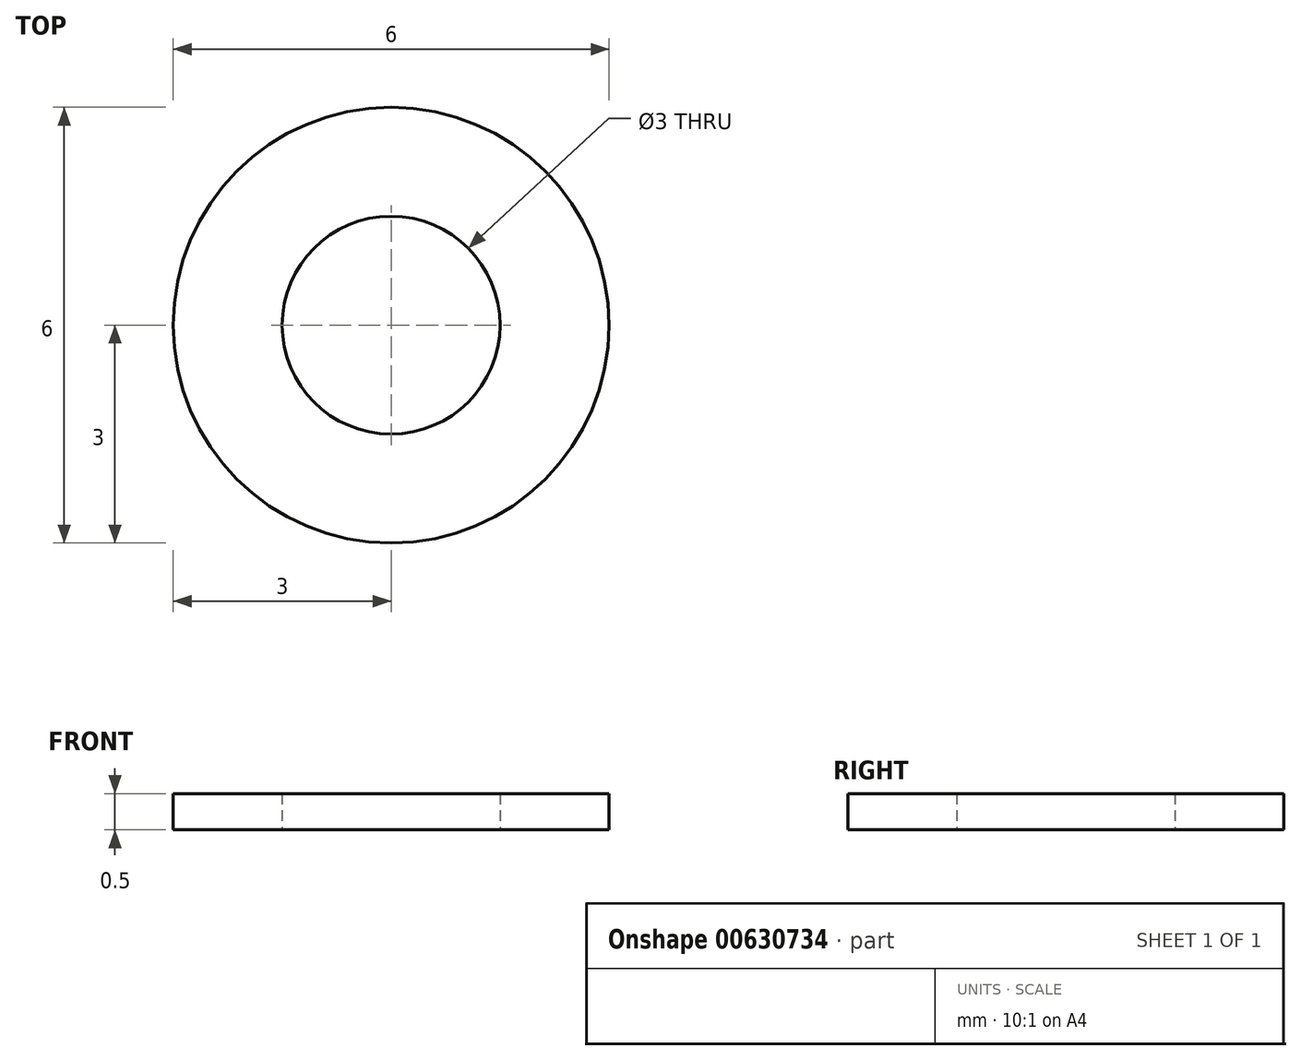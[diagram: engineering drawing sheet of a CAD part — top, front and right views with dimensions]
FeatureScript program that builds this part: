
annotation { "Feature Type Name" : "Feature", "Feature Type Description" : "" }
export const myFeature = defineFeature(function(context is Context, id is Id, definition is map)
    precondition{}
    {
        {
            var Q0;
            Q0=qCreatedBy(makeId("Top.planeOp"),FACE);
            var sketch = newSketch(context, id + "F0", { "sketchPlane" : qUnion([Q0])});
            skCircle(sketch, "E0", {"center": v(0, 0) * mm, "radius": 1.5 * mm});
            skCircle(sketch, "E1", {"center": v(0, 0) * mm, "radius": 3 * mm});
            skSolve(sketch);
        }
        {
            var Q0;
            Q0=makeQuery(id+"F0.imprint","IMPRINT",FACE,{"disambiguationData":[TD([[makeQuery(id+"F0.imprint","IMPRINT",EDGE,{"derivedFrom":sQuery(id+"F0.wireOp",EDGE,"E0")}),-1.0]])]});
            extrude(context, id + "F1", {"entities" : qUnion([Q0]), "depth" : .5 * mm, "offsetDistance" : 25 * mm});
        }
    });
